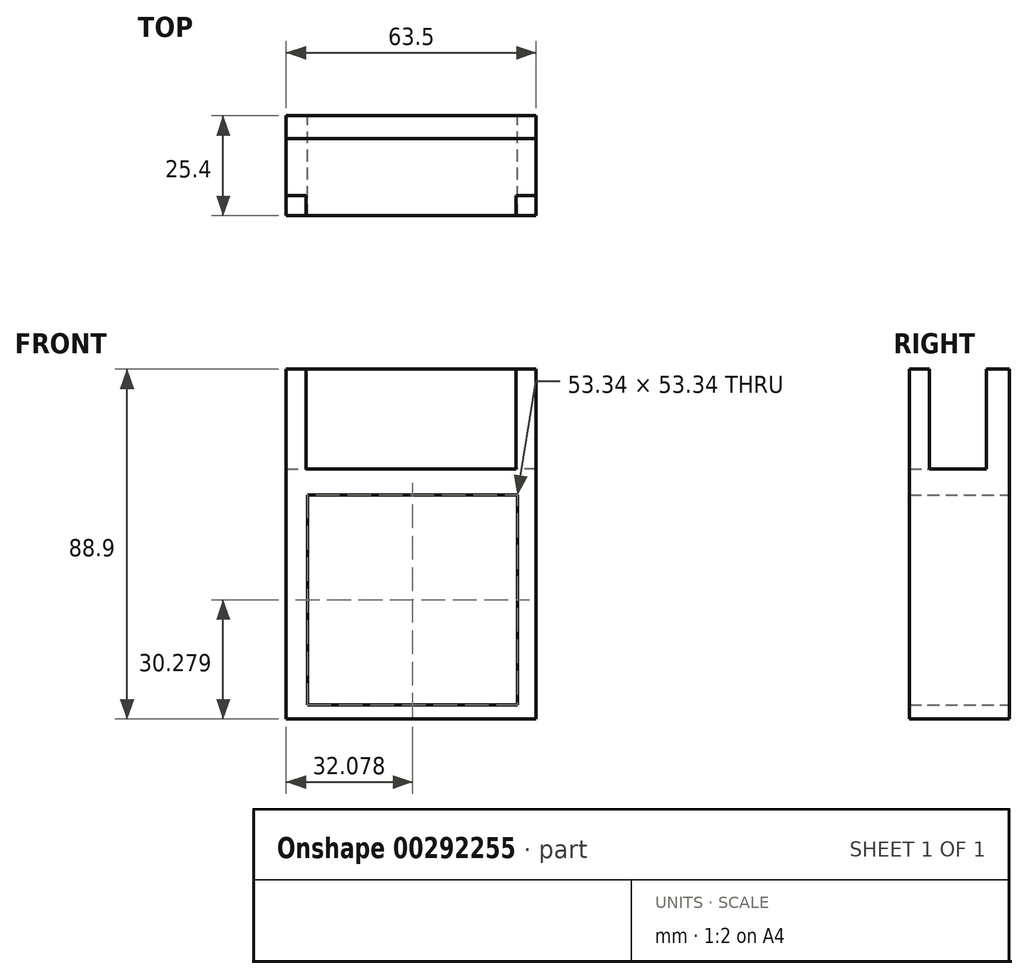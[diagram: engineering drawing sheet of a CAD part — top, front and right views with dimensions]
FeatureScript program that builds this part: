
annotation { "Feature Type Name" : "Feature", "Feature Type Description" : "" }
export const myFeature = defineFeature(function(context is Context, id is Id, definition is map)
    precondition{}
    {
        {
            var Q0;
            Q0=qCreatedBy(makeId("Front.planeOp"),FACE);
            var sketch = newSketch(context, id + "F0", { "sketchPlane" : qUnion([Q0])});
            skLineSegment(sketch, "E0.bottom", {"start": v(0, 0) * mm, "end": v(-63.5, 0) * mm});
            skLineSegment(sketch, "E0.top", {"start": v(0, 63.5) * mm, "end": v(-63.5, 63.5) * mm});
            skLineSegment(sketch, "E0.left", {"start": v(0, 0) * mm, "end": v(0, 63.5) * mm});
            skLineSegment(sketch, "E0.right", {"start": v(-63.5, 0) * mm, "end": v(-63.5, 63.5) * mm});
            skSolve(sketch);
        }
        {
            var Q0;
            Q0=makeQuery(id+"F0.imprint","IMPRINT",FACE,{"disambiguationData":[TD([[makeQuery(id+"F0.imprint","IMPRINT",EDGE,{"derivedFrom":sQuery(id+"F0.wireOp",EDGE,"E0.bottom")}),-1.0]])]});
            var sketch = newSketch(context, id + "F1", { "sketchPlane" : qUnion([Q0])});
            skLineSegment(sketch, "E1.bottom", {"start": v(-58.1, 56.95) * mm, "end": v(-4.75, 56.95) * mm});
            skLineSegment(sketch, "E1.top", {"start": v(-58.1, 3.6) * mm, "end": v(-4.75, 3.6) * mm});
            skLineSegment(sketch, "E1.left", {"start": v(-58.1, 56.95) * mm, "end": v(-58.1, 3.6) * mm});
            skLineSegment(sketch, "E1.right", {"start": v(-4.75, 56.95) * mm, "end": v(-4.75, 3.6) * mm});
            skSolve(sketch);
        }
        {
            var Q0;
            Q0=makeQuery(id+"F1.imprint","IMPRINT",FACE,{"disambiguationData":[TD([[makeQuery(id+"F1.imprint","IMPRINT",EDGE,{"derivedFrom":sQuery(id+"F1.wireOp",EDGE,"E1.bottom")}),1.0]])]});
            extrude(context, id + "F2", {"entities" : qUnion([Q0]), "depth" : 25.4 * mm});
        }
        {
            var Q0;
            Q0=makeQuery(id+"F2.opExtrude","SWEPT_FACE",FACE,{"disambiguationData":[OSD([sQuery(id+"F0.wireOp",EDGE,"E0.top")])]});
            var sketch = newSketch(context, id + "F3", { "sketchPlane" : qUnion([Q0])});
            skLineSegment(sketch, "E2.bottom", {"start": v(-63.5, 0) * mm, "end": v(0, 0) * mm});
            skLineSegment(sketch, "E2.top", {"start": v(-63.5, -5.82) * mm, "end": v(0, -5.82) * mm});
            skLineSegment(sketch, "E2.left", {"start": v(-63.5, 0) * mm, "end": v(-63.5, -5.82) * mm});
            skLineSegment(sketch, "E2.right", {"start": v(0, 0) * mm, "end": v(0, -5.82) * mm});
            skLineSegment(sketch, "E3.bottom", {"start": v(-63.5, -20.32) * mm, "end": v(-58.42, -20.32) * mm});
            skLineSegment(sketch, "E3.top", {"start": v(-63.5, -25.4) * mm, "end": v(-58.42, -25.4) * mm});
            skLineSegment(sketch, "E3.left", {"start": v(-63.5, -20.32) * mm, "end": v(-63.5, -25.4) * mm});
            skLineSegment(sketch, "E3.right", {"start": v(-58.42, -20.32) * mm, "end": v(-58.42, -25.4) * mm});
            skLineSegment(sketch, "E4.bottom", {"start": v(0, -25.4) * mm, "end": v(-5.08, -25.4) * mm});
            skLineSegment(sketch, "E4.top", {"start": v(0, -20.32) * mm, "end": v(-5.08, -20.32) * mm});
            skLineSegment(sketch, "E4.left", {"start": v(0, -25.4) * mm, "end": v(0, -20.32) * mm});
            skLineSegment(sketch, "E4.right", {"start": v(-5.08, -25.4) * mm, "end": v(-5.08, -20.32) * mm});
            skSolve(sketch);
        }
        {
            var Q0;
            Q0 = qSketchRegion(id + "F3", true);
            extrude(context, id + "F4", {"entities" : qUnion([Q0]), "operationType" : NewBodyOperationType.ADD, "depth" : 25.4 * mm});
        }
    });
